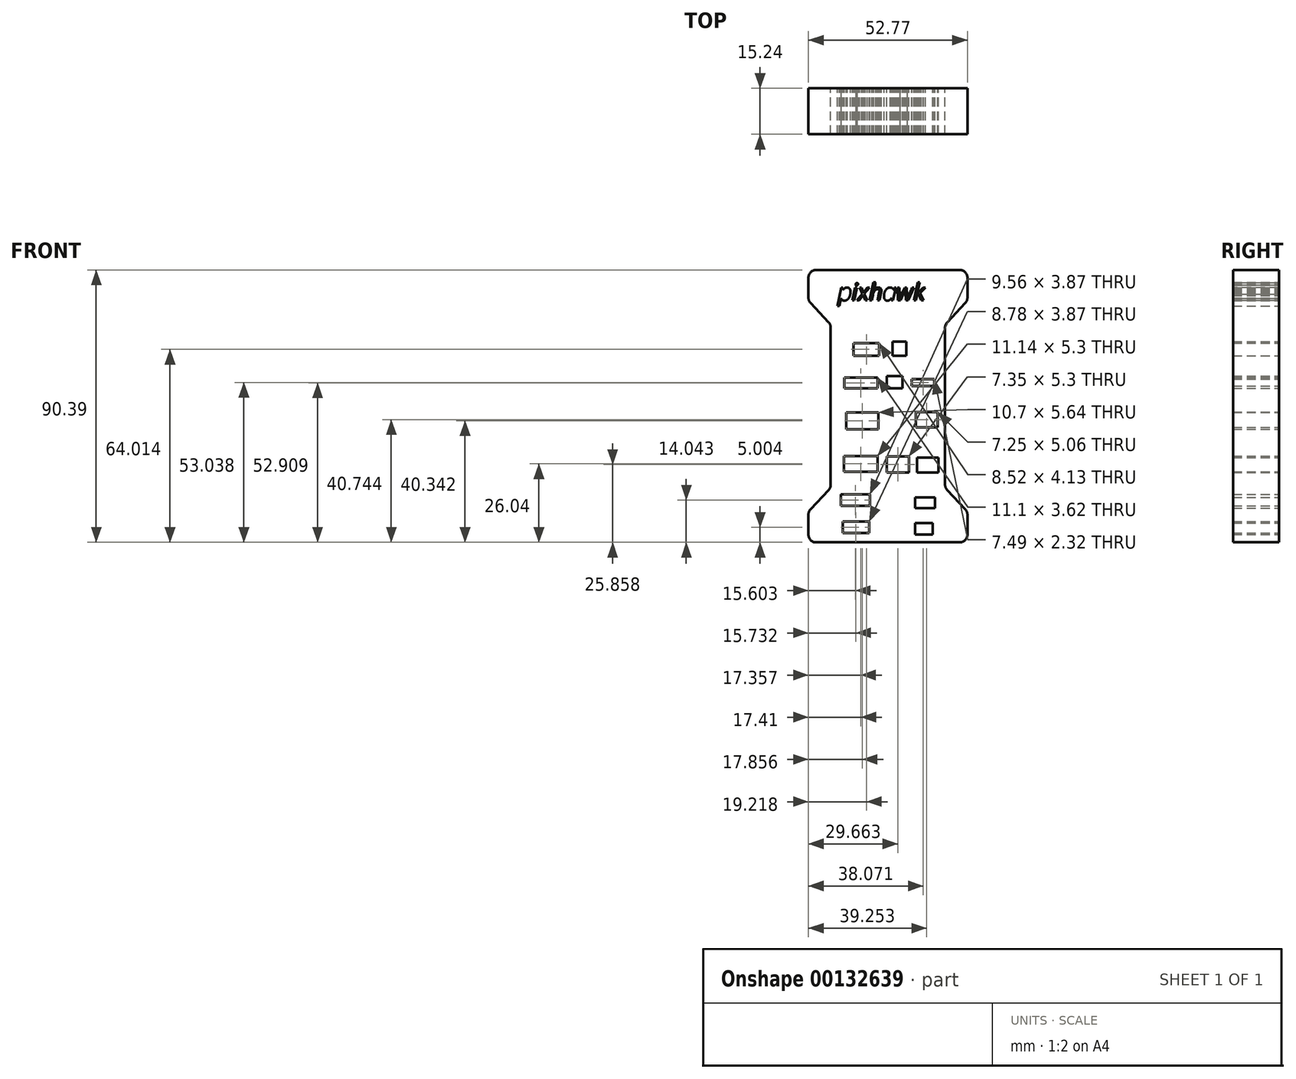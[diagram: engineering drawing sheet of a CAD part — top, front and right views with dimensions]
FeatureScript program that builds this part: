
annotation { "Feature Type Name" : "Feature", "Feature Type Description" : "" }
export const myFeature = defineFeature(function(context is Context, id is Id, definition is map)
    precondition{}
    {
        {
            var Q0;
            Q0=qCreatedBy(makeId("Front.planeOp"),FACE);
            var sketch = newSketch(context, id + "F0", { "sketchPlane" : qUnion([Q0])});
            skText(sketch, "E0", { "text": "pixhawk", "fontName": "OpenSans-Italic.ttf"});
            skLineSegment(sketch, "E1.bottom", {"start": v(-12.44, 30.78) * mm, "end": v(-3.92, 30.78) * mm});
            skLineSegment(sketch, "E1.top", {"start": v(-12.44, 26.65) * mm, "end": v(-3.92, 26.65) * mm});
            skLineSegment(sketch, "E1.left", {"start": v(-12.44, 30.78) * mm, "end": v(-12.44, 26.65) * mm});
            skLineSegment(sketch, "E1.right", {"start": v(-3.92, 30.78) * mm, "end": v(-3.92, 26.65) * mm});
            skLineSegment(sketch, "E2.bottom", {"start": v(0.47, 31.3) * mm, "end": v(5.12, 31.3) * mm});
            skLineSegment(sketch, "E2.top", {"start": v(0.47, 26.65) * mm, "end": v(5.12, 26.65) * mm});
            skLineSegment(sketch, "E2.left", {"start": v(0.47, 31.3) * mm, "end": v(0.47, 26.65) * mm});
            skLineSegment(sketch, "E2.right", {"start": v(5.12, 31.3) * mm, "end": v(5.12, 26.65) * mm});
            skLineSegment(sketch, "E3.bottom", {"start": v(-15.54, 19.42) * mm, "end": v(-4.44, 19.42) * mm});
            skLineSegment(sketch, "E3.top", {"start": v(-15.54, 15.8) * mm, "end": v(-4.44, 15.8) * mm});
            skLineSegment(sketch, "E3.left", {"start": v(-15.54, 19.42) * mm, "end": v(-15.54, 15.8) * mm});
            skLineSegment(sketch, "E3.right", {"start": v(-4.44, 19.42) * mm, "end": v(-4.44, 15.8) * mm});
            skLineSegment(sketch, "E4.bottom", {"start": v(-1.41, 19.93) * mm, "end": v(3.83, 19.93) * mm});
            skLineSegment(sketch, "E4.top", {"start": v(-1.41, 15.8) * mm, "end": v(3.83, 15.8) * mm});
            skLineSegment(sketch, "E4.left", {"start": v(-1.41, 19.93) * mm, "end": v(-1.41, 15.8) * mm});
            skLineSegment(sketch, "E4.right", {"start": v(3.83, 19.93) * mm, "end": v(3.83, 15.8) * mm});
            skLineSegment(sketch, "E5.bottom", {"start": v(6.93, 18.9) * mm, "end": v(14.42, 18.9) * mm});
            skLineSegment(sketch, "E5.top", {"start": v(6.93, 16.58) * mm, "end": v(14.42, 16.58) * mm});
            skLineSegment(sketch, "E5.left", {"start": v(6.93, 18.9) * mm, "end": v(6.93, 16.58) * mm});
            skLineSegment(sketch, "E5.right", {"start": v(14.42, 18.9) * mm, "end": v(14.42, 16.58) * mm});
            skLineSegment(sketch, "E6.bottom", {"start": v(-16.57, -19.32) * mm, "end": v(-7.02, -19.32) * mm});
            skLineSegment(sketch, "E6.top", {"start": v(-16.57, -23.2) * mm, "end": v(-7.02, -23.2) * mm});
            skLineSegment(sketch, "E6.left", {"start": v(-16.57, -19.32) * mm, "end": v(-16.57, -23.2) * mm});
            skLineSegment(sketch, "E6.right", {"start": v(-7.02, -19.32) * mm, "end": v(-7.02, -23.2) * mm});
            skLineSegment(sketch, "E7.bottom", {"start": v(-16.06, -28.36) * mm, "end": v(-7.28, -28.36) * mm});
            skLineSegment(sketch, "E7.top", {"start": v(-16.06, -32.23) * mm, "end": v(-7.28, -32.23) * mm});
            skLineSegment(sketch, "E7.left", {"start": v(-16.06, -28.36) * mm, "end": v(-16.06, -32.23) * mm});
            skLineSegment(sketch, "E7.right", {"start": v(-7.28, -28.36) * mm, "end": v(-7.28, -32.23) * mm});
            skLineSegment(sketch, "E8.bottom", {"start": v(7.96, -20.35) * mm, "end": v(14.67, -20.35) * mm});
            skLineSegment(sketch, "E8.top", {"start": v(7.96, -23.97) * mm, "end": v(14.67, -23.97) * mm});
            skLineSegment(sketch, "E8.left", {"start": v(7.96, -20.35) * mm, "end": v(7.96, -23.97) * mm});
            skLineSegment(sketch, "E8.right", {"start": v(14.67, -20.35) * mm, "end": v(14.67, -23.97) * mm});
            skLineSegment(sketch, "E9.bottom", {"start": v(7.96, -28.88) * mm, "end": v(13.9, -28.88) * mm});
            skLineSegment(sketch, "E9.top", {"start": v(7.96, -32.75) * mm, "end": v(13.9, -32.75) * mm});
            skLineSegment(sketch, "E9.left", {"start": v(7.96, -28.88) * mm, "end": v(7.96, -32.75) * mm});
            skLineSegment(sketch, "E9.right", {"start": v(13.9, -28.88) * mm, "end": v(13.9, -32.75) * mm});
            skLineSegment(sketch, "E10.bottom", {"start": v(-15.61, -6.61) * mm, "end": v(-4.47, -6.61) * mm});
            skLineSegment(sketch, "E10.top", {"start": v(-15.61, -11.9) * mm, "end": v(-4.47, -11.9) * mm});
            skLineSegment(sketch, "E10.left", {"start": v(-15.61, -6.61) * mm, "end": v(-15.61, -11.9) * mm});
            skLineSegment(sketch, "E10.right", {"start": v(-4.47, -6.61) * mm, "end": v(-4.47, -11.9) * mm});
            skLineSegment(sketch, "E11.bottom", {"start": v(-1.41, -6.8) * mm, "end": v(5.94, -6.8) * mm});
            skLineSegment(sketch, "E11.top", {"start": v(-1.41, -12.1) * mm, "end": v(5.94, -12.1) * mm});
            skLineSegment(sketch, "E11.left", {"start": v(-1.41, -6.8) * mm, "end": v(-1.41, -12.1) * mm});
            skLineSegment(sketch, "E11.right", {"start": v(5.94, -6.8) * mm, "end": v(5.94, -12.1) * mm});
            skLineSegment(sketch, "E12.bottom", {"start": v(8.68, -7.16) * mm, "end": v(15.8, -7.16) * mm});
            skLineSegment(sketch, "E12.top", {"start": v(8.68, -12.1) * mm, "end": v(15.8, -12.1) * mm});
            skLineSegment(sketch, "E12.left", {"start": v(8.68, -7.16) * mm, "end": v(8.68, -12.1) * mm});
            skLineSegment(sketch, "E12.right", {"start": v(15.8, -7.16) * mm, "end": v(15.8, -12.1) * mm});
            skLineSegment(sketch, "E13.bottom", {"start": v(-14.9, 7.86) * mm, "end": v(-4.2, 7.86) * mm});
            skLineSegment(sketch, "E13.top", {"start": v(-14.9, 2.22) * mm, "end": v(-4.2, 2.22) * mm});
            skLineSegment(sketch, "E13.left", {"start": v(-14.9, 7.86) * mm, "end": v(-14.9, 2.22) * mm});
            skLineSegment(sketch, "E13.right", {"start": v(-4.2, 7.86) * mm, "end": v(-4.2, 2.22) * mm});
            skLineSegment(sketch, "E14.bottom", {"start": v(8.23, 7.98) * mm, "end": v(15.48, 7.98) * mm});
            skLineSegment(sketch, "E14.top", {"start": v(8.23, 2.91) * mm, "end": v(15.48, 2.91) * mm});
            skLineSegment(sketch, "E14.left", {"start": v(8.23, 7.98) * mm, "end": v(8.23, 2.91) * mm});
            skLineSegment(sketch, "E14.right", {"start": v(15.48, 7.98) * mm, "end": v(15.48, 2.91) * mm});
            skLineSegment(sketch, "E15.top", {"start": v(24.97, 9.52) * mm, "end": v(-27.8, 9.52) * mm});
            skLineSegment(sketch, "E16.bottom", {"start": v(25.37, -35.3) * mm, "end": v(-27.4, -35.3) * mm});
            skLineSegment(sketch, "E16.top", {"start": v(25.37, 55.1) * mm, "end": v(-27.4, 55.1) * mm});
            skLineSegment(sketch, "E16.left", {"start": v(25.37, -35.3) * mm, "end": v(25.37, -25.07) * mm});
            skLineSegment(sketch, "E16.right", {"start": v(-27.4, -35.3) * mm, "end": v(-27.4, -25.07) * mm});
            skPoint(sketch, "E16.middle", {"position": v(-1.02, 9.9) * mm});
            skLineSegment(sketch, "E17.left", {"start": v(17.97, -17.2) * mm, "end": v(17.97, 36.99) * mm});
            skLineSegment(sketch, "E17.right", {"start": v(-20, -17.2) * mm, "end": v(-20, 36.99) * mm});
            skLineSegment(sketch, "E18", {"start": v(25.37, -25.07) * mm, "end": v(17.97, -17.2) * mm});
            skLineSegment(sketch, "E19.MirrorCS", {"start": v(-27.4, -25.07) * mm, "end": v(-20, -17.2) * mm});
            skLineSegment(sketch, "E20.MirrorCS", {"start": v(25.37, 44.87) * mm, "end": v(17.97, 36.99) * mm});
            skLineSegment(sketch, "E21.MirrorCS", {"start": v(-27.4, 44.87) * mm, "end": v(-20, 36.99) * mm});
            skLineSegment(sketch, "E22.trimOffspring", {"start": v(25.37, 44.87) * mm, "end": v(25.37, 55.1) * mm});
            skPoint(sketch, "E17.bottom.start.orphan", {"position": v(17.97, -22.79) * mm});
            skPoint(sketch, "E23.orphan", {"position": v(-20, -22.79) * mm});
            skPoint(sketch, "E17.top.start.orphan", {"position": v(17.97, 42.58) * mm});
            skPoint(sketch, "E24.orphan", {"position": v(-20, 42.58) * mm});
            skLineSegment(sketch, "E25.trimOffspring", {"start": v(-27.4, 44.87) * mm, "end": v(-27.4, 55.1) * mm});
            const initialGuessF0  = {"E0": [-0.0176, 0.04498, 1, 0, 0.00568]};
            skSetInitialGuess(sketch, initialGuessF0);
            skSolve(sketch);
        }
        {
            var Q0;
            Q0 = qSketchRegion(id + "F0", true);
            extrude(context, id + "F1", {"entities" : qUnion([Q0]), "depth" : 15.24 * mm});
        }
        {
            var Q0;
            Q0=makeQuery(id+"F1.opExtrude","SWEPT_EDGE",EDGE,{"disambiguationData":[OSD([sQuery(id+"F0.wireOp",EDGE,"E21.MirrorCS"),sQuery(id+"F0.wireOp",EDGE,"E25.trimOffspring")])]});
            var Q1;
            Q1=makeQuery(id+"F1.opExtrude","SWEPT_EDGE",EDGE,{"disambiguationData":[OSD([sQuery(id+"F0.wireOp",EDGE,"E16.top"),sQuery(id+"F0.wireOp",EDGE,"E25.trimOffspring")])]});
            var Q2;
            Q2=makeQuery(id+"F1.opExtrude","SWEPT_EDGE",EDGE,{"disambiguationData":[OSD([sQuery(id+"F0.wireOp",EDGE,"E17.right"),sQuery(id+"F0.wireOp",EDGE,"E21.MirrorCS")])]});
            var Q3;
            Q3=makeQuery(id+"F1.opExtrude","SWEPT_EDGE",EDGE,{"disambiguationData":[OSD([sQuery(id+"F0.wireOp",EDGE,"E17.right"),sQuery(id+"F0.wireOp",EDGE,"E19.MirrorCS")])]});
            var Q4;
            Q4=makeQuery(id+"F1.opExtrude","SWEPT_EDGE",EDGE,{"disambiguationData":[OSD([sQuery(id+"F0.wireOp",EDGE,"E16.right"),sQuery(id+"F0.wireOp",EDGE,"E19.MirrorCS")])]});
            var Q5;
            Q5=makeQuery(id+"F1.opExtrude","SWEPT_EDGE",EDGE,{"disambiguationData":[OSD([sQuery(id+"F0.wireOp",EDGE,"E16.bottom"),sQuery(id+"F0.wireOp",EDGE,"E16.right")])]});
            var Q6;
            Q6=makeQuery(id+"F1.opExtrude","SWEPT_EDGE",EDGE,{"disambiguationData":[OSD([sQuery(id+"F0.wireOp",EDGE,"E16.bottom"),sQuery(id+"F0.wireOp",EDGE,"E16.left")])]});
            var Q7;
            Q7=makeQuery(id+"F1.opExtrude","SWEPT_EDGE",EDGE,{"disambiguationData":[OSD([sQuery(id+"F0.wireOp",EDGE,"E16.left"),sQuery(id+"F0.wireOp",EDGE,"E18")])]});
            var Q8;
            Q8=makeQuery(id+"F1.opExtrude","SWEPT_EDGE",EDGE,{"disambiguationData":[OSD([sQuery(id+"F0.wireOp",EDGE,"E17.left"),sQuery(id+"F0.wireOp",EDGE,"E18")])]});
            var Q9;
            Q9=makeQuery(id+"F1.opExtrude","SWEPT_EDGE",EDGE,{"disambiguationData":[OSD([sQuery(id+"F0.wireOp",EDGE,"E17.left"),sQuery(id+"F0.wireOp",EDGE,"E20.MirrorCS")])]});
            var Q10;
            Q10=makeQuery(id+"F1.opExtrude","SWEPT_EDGE",EDGE,{"disambiguationData":[OSD([sQuery(id+"F0.wireOp",EDGE,"E20.MirrorCS"),sQuery(id+"F0.wireOp",EDGE,"E22.trimOffspring")])]});
            var Q11;
            Q11=makeQuery(id+"F1.opExtrude","SWEPT_EDGE",EDGE,{"disambiguationData":[OSD([sQuery(id+"F0.wireOp",EDGE,"E16.top"),sQuery(id+"F0.wireOp",EDGE,"E22.trimOffspring")])]});
            fillet(context, id + "F2", {"entities" : qUnion([Q0, Q1, Q2, Q3, Q4, Q5, Q6, Q7, Q8, Q9, Q10, Q11]), "radius" : 2.54 * mm, "tangentPropagation" : true, "allowEdgeOverflow" : false});
        }
    });
